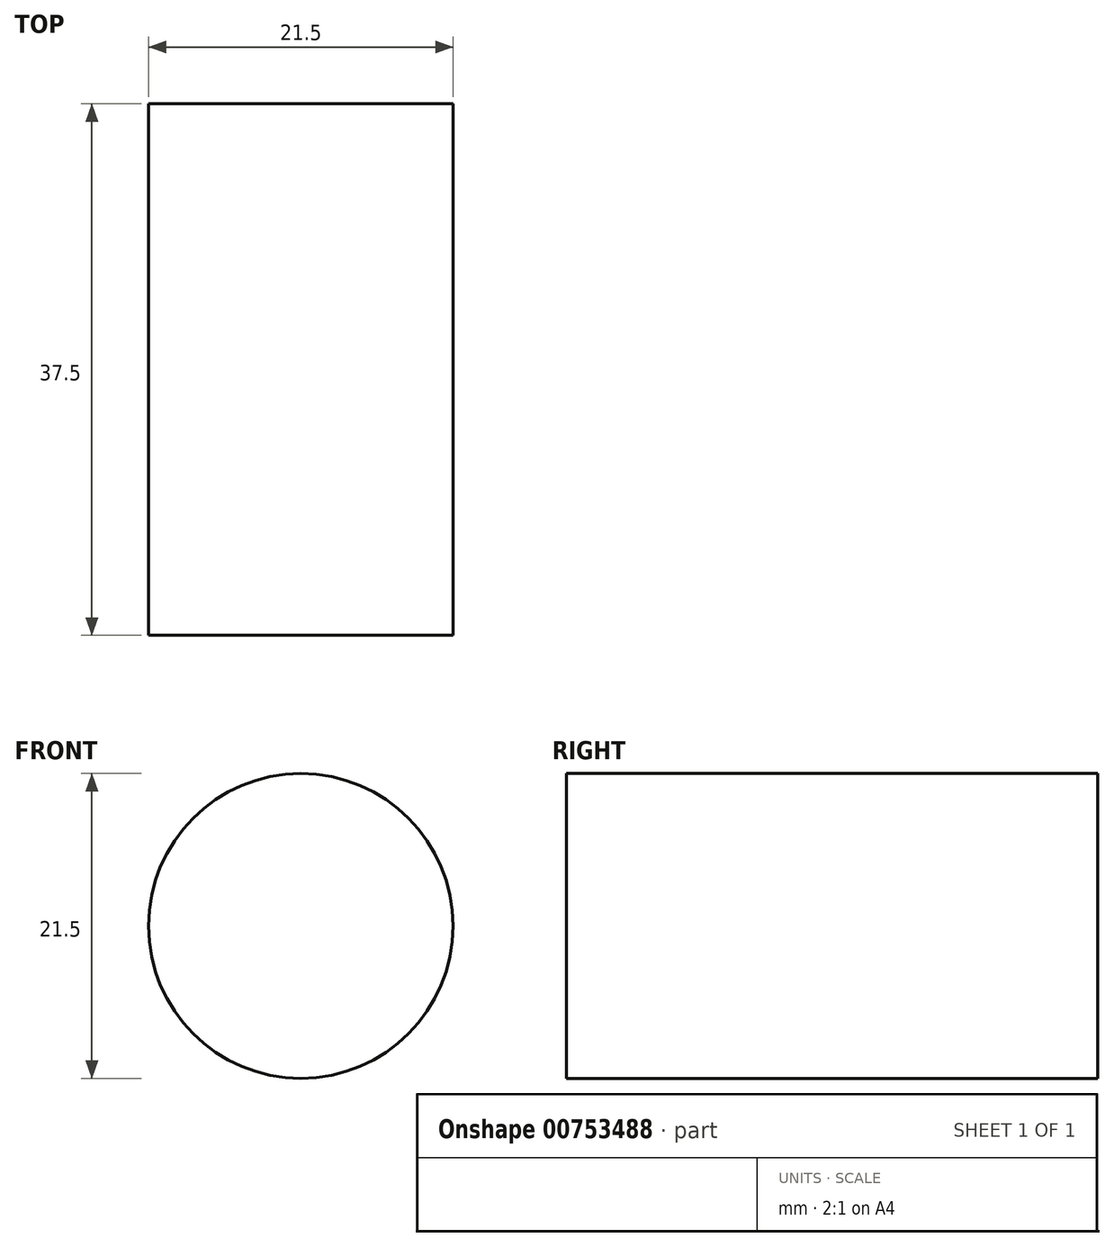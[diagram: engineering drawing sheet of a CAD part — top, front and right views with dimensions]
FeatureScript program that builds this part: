
annotation { "Feature Type Name" : "Feature", "Feature Type Description" : "" }
export const myFeature = defineFeature(function(context is Context, id is Id, definition is map)
    precondition{}
    {
        {
            var Q0;
            Q0=qCreatedBy(makeId("Front.planeOp"),FACE);
            var sketch = newSketch(context, id + "F0", { "sketchPlane" : qUnion([Q0])});
            skCircle(sketch, "E0", {"center": v(0, 0) * mm, "radius": 10.75 * mm});
            skSolve(sketch);
        }
        {
            var Q0;
            Q0=makeQuery(id+"F0.imprint","IMPRINT",FACE,{"disambiguationData":[TD([[makeQuery(id+"F0.imprint","IMPRINT",EDGE,{"derivedFrom":sQuery(id+"F0.wireOp",EDGE,"E0")}),1.0]])]});
            extrude(context, id + "F1", {"entities" : qUnion([Q0]), "depth" : 37.5 * mm, "offsetDistance" : 25.4 * mm});
        }
    });
